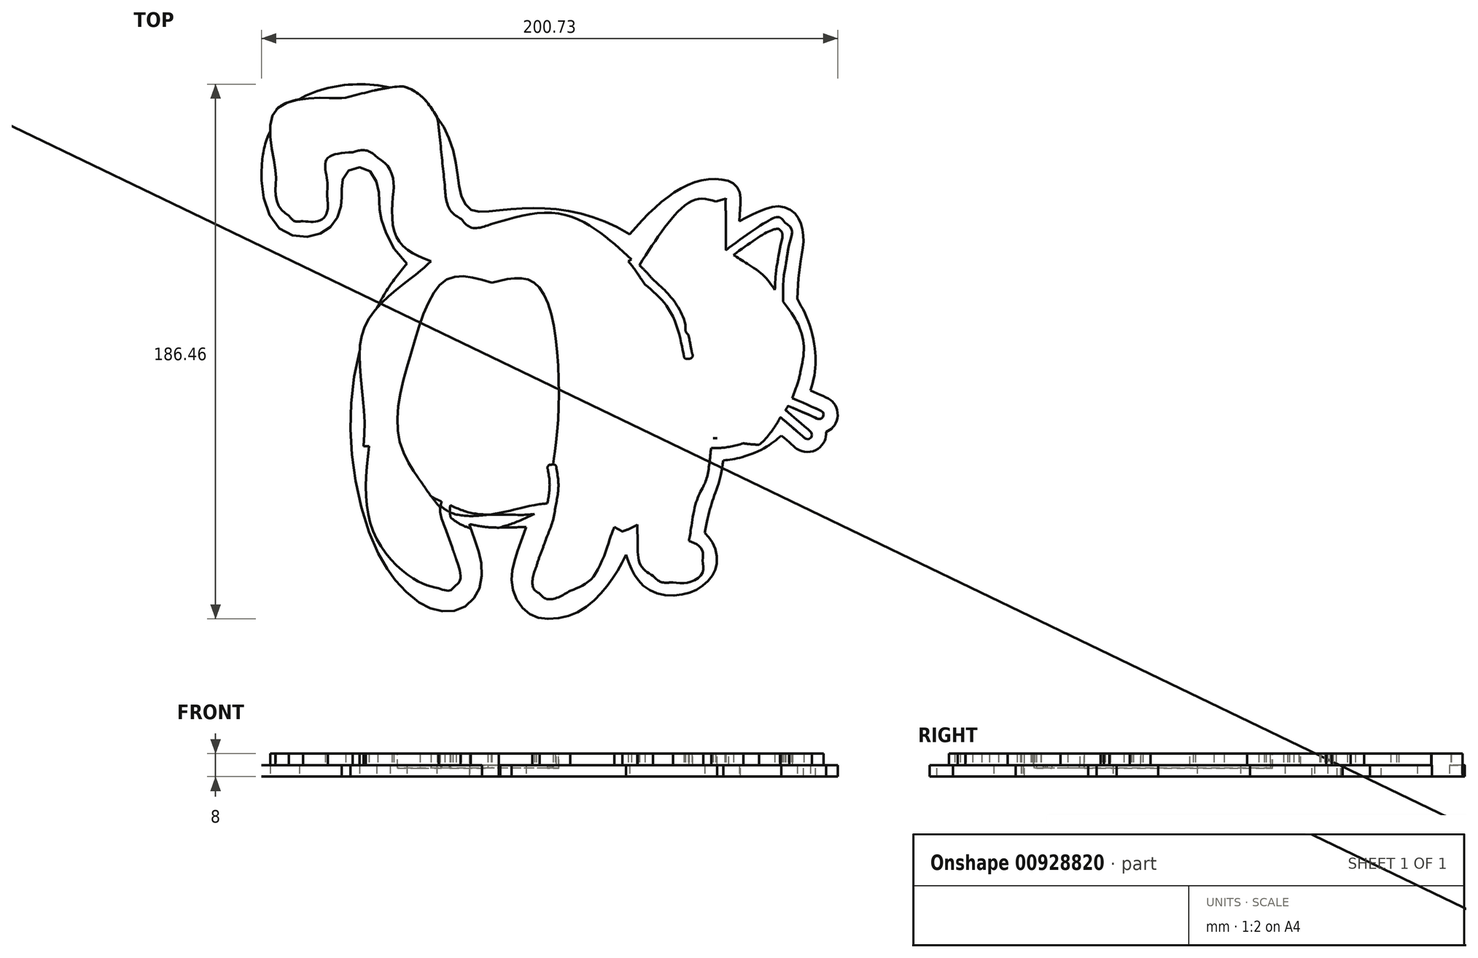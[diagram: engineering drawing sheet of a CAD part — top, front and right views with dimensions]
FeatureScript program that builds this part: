
annotation { "Feature Type Name" : "Feature", "Feature Type Description" : "" }
export const myFeature = defineFeature(function(context is Context, id is Id, definition is map)
    precondition{}
    {
        {
            var Q0;
            Q0=qCreatedBy(makeId("Top.planeOp"),FACE);
            var sketch = newSketch(context, id + "F0", { "sketchPlane" : qUnion([Q0])});
            skFitSpline(sketch, "E0", {"points": [v(100.05, -19.55) * mm, v(99.42, -17.93) * mm, v(98.2, -16.66) * mm, v(96.61, -15.96) * mm, v(96.6, -15.96) * mm, v(96.6, -15.96) * mm, v(90.96, -13.49) * mm, v(90.96, -13.48) * mm, v(90.96, -13.48) * mm, v(91.5, -11.8) * mm, v(91.97, -10.07) * mm, v(92.36, -8.28) * mm]});
            skFitSpline(sketch, "E1", {"points": [v(92.36, -8.28) * mm, v(93.69, 1.04) * mm, v(91.75, 9.81) * mm, v(86.45, 18.47) * mm]});
            skFitSpline(sketch, "E2", {"points": [v(86.45, 18.47) * mm, v(86.5, 20.98) * mm, v(86.7, 25.82) * mm, v(87.33, 29.56) * mm, v(87.33, 29.56) * mm, v(87.33, 29.56) * mm, v(87.49, 30.5) * mm, v(87.49, 30.5) * mm, v(87.49, 30.5) * mm, v(88.6, 37.13) * mm, v(89.76, 43.98) * mm, v(85.52, 48.23) * mm]});
            skFitSpline(sketch, "E3", {"points": [v(85.55, 48.2) * mm, v(84.21, 49.71) * mm, v(82.4, 50.6) * mm, v(80.32, 50.72) * mm, v(77.64, 50.9) * mm, v(74.32, 50.04) * mm, v(66.25, 45.62) * mm, v(66.25, 45.62) * mm, v(66.25, 45.62) * mm, v(66.52, 49.81) * mm, v(66.52, 49.81) * mm, v(66.52, 49.82) * mm, v(66.67, 52.13) * mm, v(66.8, 54.32) * mm, v(66.16, 56.37) * mm]});
            skFitSpline(sketch, "E4", {"points": [v(66.24, 56.23) * mm, v(64.62, 59.16) * mm, v(61.64, 60.58) * mm, v(58.04, 60.13) * mm, v(58.04, 60.13) * mm, v(58.04, 60.13) * mm, v(58.03, 60.13) * mm, v(58.02, 60.13) * mm, v(58.02, 60.13) * mm, v(58.02, 60.13) * mm]});
            skFitSpline(sketch, "E5", {"points": [v(58.04, 60.13) * mm, v(49.37, 60.78) * mm, v(39.5, 54.54) * mm, v(27.98, 41.07) * mm]});
            skFitSpline(sketch, "E6", {"points": [v(27.98, 41.07) * mm, v(17.24, 47.84) * mm, v(5.03, 50.86) * mm, v(-8.4, 50.04) * mm]});
            skFitSpline(sketch, "E7", {"points": [v(-8.4, 50.04) * mm, v(-12.56, 50.04) * mm, v(-16.9, 49.67) * mm, v(-21.3, 48.93) * mm]});
            skFitSpline(sketch, "E8", {"points": [v(-21.3, 48.93) * mm, v(-21.45, 48.9) * mm, v(-22.21, 48.75) * mm, v(-23.26, 48.75) * mm, v(-24.5, 48.75) * mm, v(-26.27, 48.97) * mm, v(-27.72, 49.98) * mm]});
            skFitSpline(sketch, "E9", {"points": [v(-27.72, 49.98) * mm, v(-29.7, 51.36) * mm, v(-30.92, 54.16) * mm, v(-31.35, 58.29) * mm]});
            skFitSpline(sketch, "E10", {"points": [v(-31.35, 58.29) * mm, v(-32.1, 65.45) * mm, v(-33.66, 74.59) * mm, v(-39.08, 81.77) * mm]});
            skFitSpline(sketch, "E11", {"points": [v(-39.08, 81.77) * mm, v(-44.85, 89.43) * mm, v(-53.9, 93.32) * mm, v(-65.99, 93.32) * mm]});
            skFitSpline(sketch, "E12", {"points": [v(-65.99, 93.32) * mm, v(-67.63, 93.32) * mm, v(-69.35, 93.25) * mm, v(-71.11, 93.1) * mm]});
            skFitSpline(sketch, "E13", {"points": [v(-71.11, 93.1) * mm, v(-80.78, 92.94) * mm, v(-100.32, 85.34) * mm, v(-100.32, 62.6) * mm, v(-100.32, 53.34) * mm, v(-98.24, 47) * mm, v(-93.96, 43.22) * mm]});
            skFitSpline(sketch, "E14", {"points": [v(-93.96, 43.22) * mm, v(-90.88, 40.5) * mm, v(-87.7, 40.1) * mm, v(-86.07, 40.1) * mm, v(-85.87, 40.1) * mm, v(-85.7, 40.1) * mm, v(-85.57, 40.1) * mm]});
            skFitSpline(sketch, "E15", {"points": [v(-85.57, 40.1) * mm, v(-77.63, 40.22) * mm, v(-72.32, 45.63) * mm, v(-72.32, 53.6) * mm, v(-72.32, 54) * mm, v(-72.32, 54.42) * mm, v(-72.33, 54.86) * mm]});
            skFitSpline(sketch, "E16", {"points": [v(-72.33, 54.86) * mm, v(-72.4, 60.63) * mm, v(-72, 62.97) * mm, v(-67.3, 64.29) * mm]});
            skFitSpline(sketch, "E17", {"points": [v(-67.3, 64.29) * mm, v(-66.87, 64.37) * mm, v(-66.46, 64.42) * mm, v(-66.06, 64.42) * mm]});
            skFitSpline(sketch, "E18", {"points": [v(-66.06, 64.42) * mm, v(-64.87, 64.42) * mm, v(-63.8, 64.03) * mm, v(-62.8, 63.22) * mm]});
            skFitSpline(sketch, "E19", {"points": [v(-62.8, 63.22) * mm, v(-60.65, 61.5) * mm, v(-59.32, 58.2) * mm, v(-59.32, 54.6) * mm, v(-59.32, 43.94) * mm, v(-55.96, 35.93) * mm, v(-49.09, 30.32) * mm]});
            skFitSpline(sketch, "E20", {"points": [v(-49.06, 31.26) * mm, v(-56.9, 22.68) * mm, v(-69.3, 4.66) * mm, v(-69.3, -23.45) * mm, v(-69.3, -65.04) * mm, v(-52.28, -85.8) * mm, v(-40.85, -89.61) * mm]});
            skFitSpline(sketch, "E21", {"points": [v(-40.85, -89.61) * mm, v(-39, -90.23) * mm, v(-37.21, -90.54) * mm, v(-35.54, -90.54) * mm]});
            skFitSpline(sketch, "E22", {"points": [v(-35.54, -90.54) * mm, v(-31.43, -90.54) * mm, v(-28.77, -88.74) * mm, v(-27.26, -87.23) * mm, v(-22.51, -82.48) * mm, v(-22.87, -74.65) * mm, v(-24.62, -69.4) * mm]});
            skFitSpline(sketch, "E23", {"points": [v(-24.62, -69.4) * mm, v(-24.96, -68.4) * mm, v(-25.35, -67.28) * mm, v(-25.77, -66.08) * mm]});
            skFitSpline(sketch, "E24", {"points": [v(-25.77, -66.08) * mm, v(-26.27, -64.66) * mm, v(-27.07, -62.37) * mm, v(-27.8, -60.06) * mm]});
            skFitSpline(sketch, "E25", {"points": [v(-27.81, -60.06) * mm, v(-23.36, -60.89) * mm, v(-18.46, -61.28) * mm, v(-13.17, -61.24) * mm, v(-11.35, -61.22) * mm, v(-9.62, -61.15) * mm, v(-8.01, -61.05) * mm]});
            skFitSpline(sketch, "E26", {"points": [v(-8.01, -61.05) * mm, v(-8.45, -62.3) * mm, v(-8.91, -63.53) * mm, v(-9.36, -64.74) * mm]});
            skFitSpline(sketch, "E27", {"points": [v(-9.36, -64.74) * mm, v(-10.33, -67.35) * mm, v(-11.25, -69.8) * mm, v(-12.03, -72.4) * mm]});
            skFitSpline(sketch, "E28", {"points": [v(-12.03, -72.4) * mm, v(-14.3, -79.95) * mm, v(-12.89, -86.47) * mm, v(-8.18, -90.3) * mm]});
            skFitSpline(sketch, "E29", {"points": [v(-8.18, -90.3) * mm, v(-6.56, -91.6) * mm, v(-3.77, -93.17) * mm, v(0.34, -93.17) * mm, v(3.74, -93.17) * mm, v(7.45, -92.08) * mm, v(11.4, -89.93) * mm]});
            skFitSpline(sketch, "E30", {"points": [v(11.4, -89.93) * mm, v(18.3, -85.62) * mm, v(23.55, -77.3) * mm, v(26.85, -70.76) * mm]});
            skFitSpline(sketch, "E31", {"points": [v(26.85, -70.76) * mm, v(27.9, -74.84) * mm, v(29.69, -78.7) * mm, v(32.65, -81.38) * mm]});
            skFitSpline(sketch, "E32", {"points": [v(32.65, -81.38) * mm, v(35.24, -83.73) * mm, v(38.48, -84.97) * mm, v(42, -84.97) * mm, v(42.42, -84.97) * mm, v(42.84, -84.95) * mm, v(43.26, -84.92) * mm]});
            skFitSpline(sketch, "E33", {"points": [v(43.26, -84.92) * mm, v(51.65, -84.78) * mm, v(58.45, -79.2) * mm, v(58.45, -72.42) * mm, v(58.45, -68.76) * mm, v(56.88, -65.47) * mm, v(54.13, -63.1) * mm]});
            skFitSpline(sketch, "E34", {"points": [v(54.13, -63.1) * mm, v(54.92, -59.03) * mm, v(56.29, -52.8) * mm, v(57.92, -48.98) * mm]});
            skFitSpline(sketch, "E35", {"points": [v(57.92, -48.98) * mm, v(59.23, -45.93) * mm, v(60.1, -41.73) * mm, v(60.66, -37.87) * mm]});
            skFitSpline(sketch, "E36", {"points": [v(60.66, -37.87) * mm, v(65.8, -37.43) * mm, v(73.93, -35.63) * mm, v(80.9, -29.2) * mm, v(80.9, -29.2) * mm, v(80.9, -29.2) * mm, v(85.7, -33.34) * mm, v(85.7, -33.34) * mm, v(85.7, -33.34) * mm, v(86.88, -34.36) * mm, v(88.39, -34.92) * mm, v(89.94, -34.92) * mm, v(91.84, -34.92) * mm, v(93.63, -34.1) * mm, v(94.87, -32.66) * mm]});
            skFitSpline(sketch, "E37", {"points": [v(94.87, -32.66) * mm, v(96, -31.35) * mm, v(96.56, -29.68) * mm, v(96.43, -27.94) * mm]});
            skFitSpline(sketch, "E38", {"points": [v(96.43, -27.94) * mm, v(97.98, -27.32) * mm, v(99.26, -26.1) * mm, v(99.95, -24.52) * mm]});
            skFitSpline(sketch, "E39", {"points": [v(99.95, -24.52) * mm, v(100.65, -22.93) * mm, v(100.69, -21.17) * mm, v(100.05, -19.55) * mm]});
            skFitSpline(sketch, "E40", {"points": [v(-20, 24.09) * mm, v(-36, 25.09) * mm, v(-48, 0.09) * mm, v(-51.98, -31.79) * mm, v(-45.1, -44.74) * mm, v(-45, -44.91) * mm, v(-45, -44.91) * mm, v(-45, -44.91) * mm]});
            skFitSpline(sketch, "E41", {"points": [v(-45, -44.91) * mm, v(-45, -44.91) * mm, v(-45, -44.91) * mm, v(-44.81, -45.11) * mm, v(-30.47, -60.36) * mm, v(0.64, -53.66) * mm]});
            skFitSpline(sketch, "E42", {"points": [v(0.64, -53.66) * mm, v(2, -48.91) * mm, v(1, -40.92) * mm, v(1, -40.91) * mm, v(1, -40.91) * mm, v(3, -24.9) * mm, v(-4, 23.09) * mm, v(-20, 24.09) * mm]});
            skFitSpline(sketch, "E43", {"points": [v(94.6, -20.54) * mm, v(94.6, -20.54) * mm, v(94.6, -20.54) * mm, v(94.34, -20.43) * mm, v(84.57, -16.14) * mm, v(84.57, -16.14) * mm, v(84.57, -16.14) * mm, v(85.75, -13.56) * mm, v(86.74, -10.62) * mm, v(87.47, -7.23) * mm, v(87.47, -7.2) * mm, v(87.48, -7.16) * mm, v(87.49, -7.13) * mm]});
            skFitSpline(sketch, "E44", {"points": [v(87.49, -7.13) * mm, v(88.7, 1.43) * mm, v(86.75, 9.5) * mm, v(81.5, 17.52) * mm]});
            skFitSpline(sketch, "E45", {"points": [v(81.5, 17.52) * mm, v(81.52, 19.24) * mm, v(81.64, 25.8) * mm, v(82.48, 30.84) * mm, v(82.48, 30.84) * mm, v(82.48, 30.84) * mm, v(82.64, 31.78) * mm, v(82.64, 31.78) * mm, v(82.64, 31.78) * mm, v(83.55, 37.16) * mm, v(84.48, 42.72) * mm, v(82.06, 45.15) * mm]});
            skFitSpline(sketch, "E46", {"points": [v(82.06, 45.15) * mm, v(80.3, 46.9) * mm, v(76.8, 46.02) * mm, v(62.53, 36.26) * mm]});
            skFitSpline(sketch, "E47", {"points": [v(62.54, 36.27) * mm, v(62.14, 36) * mm, v(61.8, 35.76) * mm, v(61.52, 35.57) * mm, v(61.51, 35.57) * mm, v(61.51, 35.62) * mm, v(61.5, 49.1) * mm, v(61.5, 49.1) * mm, v(61.5, 49.1) * mm, v(61.49, 53.01) * mm, v(61.48, 55.6) * mm, v(57.98, 55.59) * mm, v(57.87, 55.59) * mm, v(57.74, 55.6) * mm, v(57.57, 55.62) * mm]});
            skFitSpline(sketch, "E48", {"points": [v(57.59, 55.61) * mm, v(54.51, 55.88) * mm, v(45.27, 56.66) * mm, v(28.65, 32.24) * mm]});
            skFitSpline(sketch, "E49", {"points": [v(28.65, 32.24) * mm, v(18.35, 41.12) * mm, v(2.62, 48.38) * mm, v(-20.25, 44.57) * mm]});
            skFitSpline(sketch, "E50", {"points": [v(-20.25, 44.57) * mm, v(-20.3, 44.55) * mm, v(-26.05, 43.17) * mm, v(-30.65, 46.38) * mm]});
            skFitSpline(sketch, "E51", {"points": [v(-30.65, 46.38) * mm, v(-33.87, 48.63) * mm, v(-35.8, 52.63) * mm, v(-36.4, 58.27) * mm]});
            skFitSpline(sketch, "E52", {"points": [v(-36.4, 58.27) * mm, v(-38.1, 74.54) * mm, v(-43.55, 90.86) * mm, v(-70.95, 88.61) * mm]});
            skFitSpline(sketch, "E53", {"points": [v(-70.95, 88.61) * mm, v(-76.22, 88.57) * mm, v(-95.38, 84.2) * mm, v(-95.38, 63.11) * mm, v(-95.38, 55.46) * mm, v(-93.81, 50.2) * mm, v(-90.72, 47.47) * mm]});
            skFitSpline(sketch, "E54", {"points": [v(-90.72, 47.47) * mm, v(-88.54, 45.55) * mm, v(-86.37, 45.57) * mm, v(-85.81, 45.61) * mm]});
            skFitSpline(sketch, "E55", {"points": [v(-85.81, 45.61) * mm, v(-80.53, 45.64) * mm, v(-77.38, 48.81) * mm, v(-77.38, 54.11) * mm, v(-77.38, 54.48) * mm, v(-77.39, 54.88) * mm, v(-77.4, 55.3) * mm]});
            skFitSpline(sketch, "E56", {"points": [v(-77.4, 55.3) * mm, v(-77.46, 60.31) * mm, v(-77.56, 67.19) * mm, v(-68.56, 69.65) * mm]});
            skFitSpline(sketch, "E57", {"points": [v(-68.56, 69.65) * mm, v(-65.33, 70.36) * mm, v(-62.28, 69.66) * mm, v(-59.74, 67.63) * mm]});
            skFitSpline(sketch, "E58", {"points": [v(-59.74, 67.63) * mm, v(-56.39, 64.94) * mm, v(-54.38, 60.26) * mm, v(-54.38, 55.11) * mm, v(-54.38, 43.67) * mm, v(-50.32, 36.34) * mm, v(-41.25, 31.6) * mm]});
            skFitSpline(sketch, "E59", {"points": [v(-41.25, 31.6) * mm, v(-47.13, 26.46) * mm, v(-64.38, 8.6) * mm, v(-64.38, -23.89) * mm, v(-64.38, -62.56) * mm, v(-49.03, -82.09) * mm, v(-39.36, -85.31) * mm]});
            skFitSpline(sketch, "E60", {"points": [v(-39.36, -85.31) * mm, v(-37.93, -85.79) * mm, v(-36.7, -85.98) * mm, v(-35.63, -85.98) * mm]});
            skFitSpline(sketch, "E61", {"points": [v(-35.63, -85.98) * mm, v(-33.33, -85.98) * mm, v(-31.83, -85.07) * mm, v(-30.9, -84.14) * mm]});
            skFitSpline(sketch, "E62", {"points": [v(-30.9, -84.14) * mm, v(-27.95, -81.2) * mm, v(-28.05, -75.63) * mm, v(-29.46, -71.42) * mm]});
            skFitSpline(sketch, "E63", {"points": [v(-29.46, -71.42) * mm, v(-29.78, -70.45) * mm, v(-30.17, -69.35) * mm, v(-30.58, -68.18) * mm]});
            skFitSpline(sketch, "E64", {"points": [v(-30.58, -68.18) * mm, v(-32.12, -63.8) * mm, v(-34.53, -56.92) * mm, v(-34.48, -53.5) * mm]});
            skFitSpline(sketch, "E65", {"points": [v(-34.48, -53.5) * mm, v(-27.6, -56.08) * mm, v(-19.8, -56.8) * mm, v(-13.26, -56.8) * mm, v(-8.06, -56.8) * mm, v(-3.66, -56.36) * mm, v(-1.16, -56.03) * mm]});
            skFitSpline(sketch, "E66", {"points": [v(-1.16, -56.03) * mm, v(-2.09, -59.9) * mm, v(-3.43, -63.54) * mm, v(-4.76, -67.1) * mm]});
            skFitSpline(sketch, "E67", {"points": [v(-4.76, -67.1) * mm, v(-5.7, -69.63) * mm, v(-6.58, -72) * mm, v(-7.32, -74.46) * mm]});
            skFitSpline(sketch, "E68", {"points": [v(-7.32, -74.46) * mm, v(-8.97, -79.97) * mm, v(-8.17, -84.55) * mm, v(-5.1, -87.03) * mm]});
            skFitSpline(sketch, "E69", {"points": [v(-5.1, -87.03) * mm, v(-4.1, -87.85) * mm, v(-2.37, -88.79) * mm, v(0.26, -88.79) * mm, v(2.47, -88.79) * mm, v(5.32, -88.12) * mm, v(8.91, -86.16) * mm]});
            skFitSpline(sketch, "E70", {"points": [v(8.91, -86.16) * mm, v(17.59, -80.74) * mm, v(23.66, -67.02) * mm, v(25.43, -62.65) * mm]});
            skFitSpline(sketch, "E71", {"points": [v(25.43, -62.65) * mm, v(26.4, -62.3) * mm, v(28.3, -61.54) * mm, v(30.64, -60.24) * mm]});
            skFitSpline(sketch, "E72", {"points": [v(30.64, -60.24) * mm, v(30.76, -65.7) * mm, v(31.73, -74.12) * mm, v(36.18, -78.15) * mm]});
            skFitSpline(sketch, "E73", {"points": [v(36.18, -78.15) * mm, v(37.86, -79.67) * mm, v(39.87, -80.44) * mm, v(42.17, -80.44) * mm, v(42.5, -80.44) * mm, v(42.85, -80.42) * mm, v(43.2, -80.39) * mm]});
            skFitSpline(sketch, "E74", {"points": [v(43.05, -80.4) * mm, v(48.7, -80.36) * mm, v(53.47, -76.94) * mm, v(53.47, -72.9) * mm, v(53.47, -69.83) * mm, v(51.73, -67.35) * mm, v(48.65, -65.94) * mm]});
            skFitSpline(sketch, "E75", {"points": [v(48.68, -65.95) * mm, v(49.24, -62.62) * mm, v(51, -53.03) * mm, v(53.38, -47.5) * mm]});
            skFitSpline(sketch, "E76", {"points": [v(53.38, -47.5) * mm, v(54.77, -44.33) * mm, v(55.79, -39) * mm, v(56.4, -33.46) * mm]});
            skFitSpline(sketch, "E77", {"points": [v(56.3, -33.48) * mm, v(56.63, -33.5) * mm, v(57.14, -33.53) * mm, v(57.8, -33.53) * mm, v(62.2, -33.52) * mm, v(72.96, -32.44) * mm, v(80.57, -22.78) * mm, v(80.57, -22.78) * mm, v(80.57, -22.78) * mm, v(89.02, -30.05) * mm, v(89.02, -30.05) * mm, v(89.02, -30.05) * mm, v(89.3, -30.3) * mm, v(89.66, -30.42) * mm, v(90, -30.42) * mm, v(90.42, -30.41) * mm, v(90.84, -30.24) * mm, v(91.14, -29.9) * mm]});
            skFitSpline(sketch, "E78", {"points": [v(91.14, -29.9) * mm, v(91.68, -29.27) * mm, v(91.6, -28.33) * mm, v(90.98, -27.78) * mm, v(90.98, -27.78) * mm, v(90.96, -27.76) * mm, v(82.35, -20.33) * mm, v(82.33, -20.3) * mm, v(82.33, -20.3) * mm, v(82.63, -19.83) * mm, v(82.93, -19.34) * mm, v(83.21, -18.83) * mm, v(83.21, -18.83) * mm, v(83.24, -18.84) * mm, v(93.38, -23.28) * mm, v(93.4, -23.29) * mm, v(93.4, -23.3) * mm, v(93.6, -23.37) * mm, v(93.8, -23.41) * mm, v(94, -23.41) * mm, v(94.58, -23.41) * mm, v(95.13, -23.08) * mm, v(95.37, -22.52) * mm]});
            skFitSpline(sketch, "E79", {"points": [v(95.37, -22.52) * mm, v(95.7, -21.76) * mm, v(95.36, -20.87) * mm, v(94.6, -20.54) * mm]});
            skFitSpline(sketch, "E80", {"points": [v(80.08, 42.86) * mm, v(81.2, 41.27) * mm, v(80.3, 35.9) * mm, v(79.68, 32.29) * mm, v(79.68, 32.28) * mm, v(79.68, 32.28) * mm, v(79.52, 31.33) * mm, v(79.52, 31.33) * mm, v(79.52, 31.33) * mm, v(78.99, 28.14) * mm, v(78.74, 24.46) * mm, v(78.61, 21.63) * mm]});
            skFitSpline(sketch, "E81", {"points": [v(78.66, 21.58) * mm, v(74.42, 26.84) * mm, v(68.01, 31.38) * mm, v(64.2, 33.82) * mm]});
            skFitSpline(sketch, "E82", {"points": [v(64.2, 33.82) * mm, v(75.54, 41.54) * mm, v(79.02, 42.85) * mm, v(80.08, 42.86) * mm]});
            skFitSpline(sketch, "E83", {"points": [v(56.8, -30.09) * mm, v(57.45, -24.16) * mm, v(57.63, -18.41) * mm, v(57.21, -15.3) * mm]});
            skFitSpline(sketch, "E84", {"points": [v(57.21, -15.3) * mm, v(57.08, -14.48) * mm, v(56.3, -13.92) * mm, v(55.49, -14.06) * mm]});
            skFitSpline(sketch, "E85", {"points": [v(55.49, -14.06) * mm, v(54.67, -14.2) * mm, v(54.12, -14.98) * mm, v(54.26, -15.8) * mm]});
            skFitSpline(sketch, "E86", {"points": [v(54.26, -15.8) * mm, v(55.17, -21.85) * mm, v(53.8, -39.35) * mm, v(50.85, -45.9) * mm]});
            skFitSpline(sketch, "E87", {"points": [v(50.85, -45.9) * mm, v(47.84, -53) * mm, v(45.9, -65.75) * mm, v(45.82, -66.29) * mm]});
            skFitSpline(sketch, "E88", {"points": [v(45.82, -66.29) * mm, v(45.7, -67) * mm, v(46.13, -67.7) * mm, v(46.82, -67.94) * mm]});
            skFitSpline(sketch, "E89", {"points": [v(46.56, -67.86) * mm, v(48.39, -68.4) * mm, v(50.59, -69.63) * mm, v(50.67, -72.31) * mm, v(50.73, -74.4) * mm, v(47.53, -76.91) * mm, v(43.31, -77.04) * mm, v(43.26, -77.04) * mm, v(43.21, -77.04) * mm, v(43.16, -77.05) * mm]});
            skFitSpline(sketch, "E90", {"points": [v(43.16, -77.05) * mm, v(41.26, -77.26) * mm, v(39.69, -76.8) * mm, v(38.37, -75.63) * mm]});
            skFitSpline(sketch, "E91", {"points": [v(38.37, -75.63) * mm, v(34.21, -71.92) * mm, v(33.7, -62.5) * mm, v(33.67, -58.63) * mm, v(33.67, -58.48) * mm, v(33.64, -58.34) * mm, v(33.6, -58.21) * mm]});
            skFitSpline(sketch, "E92", {"points": [v(33.6, -58.21) * mm, v(39.18, -54.54) * mm, v(45.84, -48.25) * mm, v(48.71, -38.1) * mm]});
            skFitSpline(sketch, "E93", {"points": [v(48.71, -38.1) * mm, v(48.93, -37.3) * mm, v(48.46, -36.48) * mm, v(47.67, -36.26) * mm]});
            skFitSpline(sketch, "E94", {"points": [v(47.67, -36.26) * mm, v(46.87, -36.04) * mm, v(46.04, -36.5) * mm, v(45.82, -37.3) * mm]});
            skFitSpline(sketch, "E95", {"points": [v(45.82, -37.3) * mm, v(42.3, -49.82) * mm, v(32.13, -56.07) * mm, v(26.98, -58.5) * mm]});
            skFitSpline(sketch, "E96", {"points": [v(26.98, -58.5) * mm, v(29.59, -51.06) * mm, v(34.55, -34.09) * mm, v(30.56, -22.16) * mm]});
            skFitSpline(sketch, "E97", {"points": [v(30.56, -22.16) * mm, v(30.3, -21.38) * mm, v(29.45, -20.95) * mm, v(28.66, -21.2) * mm]});
            skFitSpline(sketch, "E98", {"points": [v(28.66, -21.2) * mm, v(27.88, -21.47) * mm, v(27.45, -22.32) * mm, v(27.71, -23.1) * mm]});
            skFitSpline(sketch, "E99", {"points": [v(27.71, -23.1) * mm, v(32.46, -37.4) * mm, v(22.82, -60.81) * mm, v(22.72, -61.07) * mm]});
            skFitSpline(sketch, "E100", {"points": [v(22.72, -61.07) * mm, v(21.58, -63.88) * mm, v(15.49, -78.18) * mm, v(7.31, -83.25) * mm]});
            skFitSpline(sketch, "E101", {"points": [v(7.31, -83.25) * mm, v(2.74, -85.73) * mm, v(-1.13, -86.12) * mm, v(-3.3, -84.34) * mm]});
            skFitSpline(sketch, "E102", {"points": [v(-3.3, -84.34) * mm, v(-5.34, -82.68) * mm, v(-5.8, -79.18) * mm, v(-4.52, -74.96) * mm]});
            skFitSpline(sketch, "E103", {"points": [v(-4.52, -74.96) * mm, v(-3.81, -72.6) * mm, v(-2.94, -70.26) * mm, v(-2.02, -67.79) * mm]});
            skFitSpline(sketch, "E104", {"points": [v(-2.02, -67.79) * mm, v(-0.49, -63.65) * mm, v(1.16, -59.22) * mm, v(2.11, -54.3) * mm]});
            skFitSpline(sketch, "E105", {"points": [v(2.11, -54.3) * mm, v(2.9, -50.13) * mm, v(3.19, -45.6) * mm, v(2.47, -40.61) * mm]});
            skFitSpline(sketch, "E106", {"points": [v(2.47, -40.61) * mm, v(2.36, -39.8) * mm, v(1.6, -39.22) * mm, v(0.78, -39.34) * mm]});
            skFitSpline(sketch, "E107", {"points": [v(0.78, -39.34) * mm, v(-0.04, -39.46) * mm, v(-0.61, -40.22) * mm, v(-0.5, -41.04) * mm]});
            skFitSpline(sketch, "E108", {"points": [v(-0.5, -41.04) * mm, v(0.12, -45.32) * mm, v(-0.05, -49.2) * mm, v(-0.66, -52.85) * mm]});
            skFitSpline(sketch, "E109", {"points": [v(-0.66, -52.85) * mm, v(-6.2, -53.62) * mm, v(-32.84, -56.57) * mm, v(-43.87, -43.83) * mm]});
            skFitSpline(sketch, "E110", {"points": [v(-43.87, -43.83) * mm, v(-44.4, -43.2) * mm, v(-45.36, -43.14) * mm, v(-45.98, -43.68) * mm]});
            skFitSpline(sketch, "E111", {"points": [v(-45.98, -43.68) * mm, v(-46.6, -44.22) * mm, v(-46.68, -45.17) * mm, v(-46.13, -45.8) * mm]});
            skFitSpline(sketch, "E112", {"points": [v(-46.13, -45.8) * mm, v(-43.75, -48.54) * mm, v(-40.77, -50.63) * mm, v(-37.48, -52.2) * mm]});
            skFitSpline(sketch, "E113", {"points": [v(-37.48, -52.2) * mm, v(-38.03, -55.8) * mm, v(-36.09, -61.8) * mm, v(-33.53, -69.1) * mm]});
            skFitSpline(sketch, "E114", {"points": [v(-33.53, -69.1) * mm, v(-33.12, -70.25) * mm, v(-32.74, -71.33) * mm, v(-32.42, -72.29) * mm]});
            skFitSpline(sketch, "E115", {"points": [v(-32.42, -72.29) * mm, v(-31.34, -75.54) * mm, v(-31.22, -80.03) * mm, v(-33.14, -81.94) * mm, v(-34.25, -83.06) * mm, v(-36.07, -83.2) * mm, v(-38.53, -82.39) * mm]});
            skFitSpline(sketch, "E116", {"points": [v(-38.5, -82.4) * mm, v(-46, -79.9) * mm, v(-61.48, -62.3) * mm, v(-61.48, -23.82) * mm]});
            skFitSpline(sketch, "E117", {"points": [v(-61.48, -23.82) * mm, v(-61.48, 9.58) * mm, v(-42, 27.26) * mm, v(-38.28, 30.32) * mm]});
            skFitSpline(sketch, "E118", {"points": [v(-38.28, 30.32) * mm, v(-34.83, 29.12) * mm, v(-25.05, 26.34) * mm, v(-16.42, 29.79) * mm]});
            skFitSpline(sketch, "E119", {"points": [v(-16.42, 29.79) * mm, v(-15.65, 30.1) * mm, v(-15.28, 30.97) * mm, v(-15.59, 31.74) * mm]});
            skFitSpline(sketch, "E120", {"points": [v(-15.59, 31.74) * mm, v(-15.9, 32.5) * mm, v(-16.77, 32.88) * mm, v(-17.54, 32.57) * mm]});
            skFitSpline(sketch, "E121", {"points": [v(-17.54, 32.57) * mm, v(-25.95, 29.2) * mm, v(-36.14, 32.71) * mm, v(-38.05, 33.42) * mm]});
            skFitSpline(sketch, "E122", {"points": [v(-38.05, 33.42) * mm, v(-38.05, 33.43) * mm, v(-38.05, 33.43) * mm, v(-38.06, 33.43) * mm]});
            skFitSpline(sketch, "E123", {"points": [v(-38.05, 33.42) * mm, v(-47.24, 37.6) * mm, v(-51.17, 44.08) * mm, v(-51.17, 55.06) * mm, v(-51.17, 61.1) * mm, v(-53.59, 66.66) * mm, v(-57.65, 69.92) * mm]});
            skFitSpline(sketch, "E124", {"points": [v(-57.65, 69.92) * mm, v(-60.88, 72.5) * mm, v(-64.9, 73.43) * mm, v(-69.06, 72.5) * mm]});
            skFitSpline(sketch, "E125", {"points": [v(-69.06, 72.5) * mm, v(-80.37, 69.42) * mm, v(-80.25, 60.17) * mm, v(-80.18, 55.2) * mm]});
            skFitSpline(sketch, "E126", {"points": [v(-80.18, 55.2) * mm, v(-80.17, 54.8) * mm, v(-80.17, 54.42) * mm, v(-80.17, 54.06) * mm, v(-80.17, 50.36) * mm, v(-81.97, 48.56) * mm, v(-85.67, 48.56) * mm, v(-85.7, 48.56) * mm, v(-85.78, 48.55) * mm, v(-85.82, 48.55) * mm]});
            skFitSpline(sketch, "E127", {"points": [v(-85.82, 48.55) * mm, v(-85.88, 48.54) * mm, v(-87.2, 48.45) * mm, v(-88.6, 49.74) * mm]});
            skFitSpline(sketch, "E128", {"points": [v(-88.6, 49.74) * mm, v(-90.22, 51.23) * mm, v(-92.16, 54.75) * mm, v(-92.17, 63.05) * mm, v(-92.18, 84.23) * mm, v(-70.9, 85.56) * mm, v(-70.68, 85.56) * mm, v(-70.63, 85.56) * mm, v(-70.6, 85.56) * mm, v(-70.55, 85.57) * mm]});
            skFitSpline(sketch, "E129", {"points": [v(-70.55, 85.57) * mm, v(-47.13, 87.51) * mm, v(-41.06, 75.92) * mm, v(-39.17, 57.9) * mm]});
            skFitSpline(sketch, "E130", {"points": [v(-39.17, 57.9) * mm, v(-38.48, 51.36) * mm, v(-36.13, 46.64) * mm, v(-32.17, 43.87) * mm]});
            skFitSpline(sketch, "E131", {"points": [v(-32.17, 43.87) * mm, v(-26.69, 40.04) * mm, v(-20.15, 41.4) * mm, v(-19.38, 41.59) * mm]});
            skFitSpline(sketch, "E132", {"points": [v(-19.38, 41.59) * mm, v(2.4, 45.2) * mm, v(20.14, 39.14) * mm, v(33.36, 23.55) * mm]});
            skFitSpline(sketch, "E133", {"points": [v(33.36, 23.55) * mm, v(43.3, 11.83) * mm, v(46.85, -1.19) * mm, v(46.88, -1.32) * mm]});
            skFitSpline(sketch, "E134", {"points": [v(46.88, -1.32) * mm, v(47.06, -1.99) * mm, v(47.67, -2.43) * mm, v(48.33, -2.43) * mm, v(48.46, -2.43) * mm, v(48.59, -2.42) * mm, v(48.71, -2.38) * mm]});
            skFitSpline(sketch, "E135", {"points": [v(48.71, -2.38) * mm, v(49.52, -2.17) * mm, v(50, -1.35) * mm, v(49.78, -0.55) * mm]});
            skFitSpline(sketch, "E136", {"points": [v(49.78, -0.55) * mm, v(49.64, 0) * mm, v(46.15, 13.19) * mm, v(35.86, 25.48) * mm]});
            skFitSpline(sketch, "E137", {"points": [v(35.86, 25.48) * mm, v(34.52, 27.07) * mm, v(33.03, 28.69) * mm, v(31.38, 30.28) * mm]});
            skFitSpline(sketch, "E138", {"points": [v(31.38, 30.28) * mm, v(41.99, 45.66) * mm, v(50.95, 53.14) * mm, v(58, 52.47) * mm]});
            skFitSpline(sketch, "E139", {"points": [v(58, 52.47) * mm, v(58.17, 51.97) * mm, v(58.18, 50.46) * mm, v(58.2, 49) * mm, v(58.2, 48.99) * mm, v(58.2, 48.98) * mm, v(58.35, 34.02) * mm, v(58.35, 34) * mm, v(58.35, 33.99) * mm, v(58.36, 33.43) * mm, v(58.67, 32.93) * mm, v(59.16, 32.68) * mm]});
            skFitSpline(sketch, "E140", {"points": [v(59.16, 32.68) * mm, v(59.3, 32.6) * mm, v(73.92, 24.94) * mm, v(78.75, 16.5) * mm, v(78.77, 16.46) * mm, v(78.79, 16.43) * mm, v(78.8, 16.4) * mm]});
            skFitSpline(sketch, "E141", {"points": [v(78.8, 16.4) * mm, v(83.91, 8.97) * mm, v(85.9, 1.5) * mm, v(84.9, -6.42) * mm]});
            skFitSpline(sketch, "E142", {"points": [v(84.9, -6.42) * mm, v(79.45, -31.1) * mm, v(59.83, -30.35) * mm, v(56.8, -30.09) * mm]});
            skFitSpline(sketch, "E143", {"points": [v(76.5, 4.59) * mm, v(74.84, 4.59) * mm, v(73.5, 2.8) * mm, v(73.5, 0.59) * mm, v(73.5, -1.62) * mm, v(74.84, -3.41) * mm, v(76.5, -3.41) * mm, v(78.16, -3.41) * mm, v(79.5, -1.62) * mm, v(79.5, 0.59) * mm, v(79.5, 2.8) * mm, v(78.16, 4.59) * mm, v(76.5, 4.59) * mm]});
            skFitSpline(sketch, "E144", {"points": [v(51, 13.59) * mm, v(49.07, 13.59) * mm, v(47.5, 11.8) * mm, v(47.5, 9.59) * mm, v(47.5, 7.38) * mm, v(49.07, 5.59) * mm, v(51, 5.59) * mm, v(52.93, 5.59) * mm, v(54.5, 7.38) * mm, v(54.5, 9.59) * mm, v(54.5, 11.8) * mm, v(52.93, 13.59) * mm, v(51, 13.59) * mm]});
            skFitSpline(sketch, "E145", {"points": [v(71.41, -3.47) * mm, v(70.62, -3.25) * mm, v(69.79, -3.7) * mm, v(69.56, -4.5) * mm]});
            skFitSpline(sketch, "E146", {"points": [v(69.56, -4.49) * mm, v(69.2, -5.75) * mm, v(68.86, -6.15) * mm, v(68.74, -6.26) * mm]});
            skFitSpline(sketch, "E147", {"points": [v(68.74, -6.26) * mm, v(68.2, -6.08) * mm, v(67.05, -4.63) * mm, v(66.34, -3.23) * mm]});
            skFitSpline(sketch, "E148", {"points": [v(66.34, -3.23) * mm, v(66.13, -2.8) * mm, v(65.72, -2.5) * mm, v(65.24, -2.42) * mm]});
            skFitSpline(sketch, "E149", {"points": [v(65.24, -2.42) * mm, v(64.77, -2.34) * mm, v(64.28, -2.5) * mm, v(63.94, -2.84) * mm]});
            skFitSpline(sketch, "E150", {"points": [v(63.94, -2.84) * mm, v(62.31, -4.47) * mm, v(60.88, -5.29) * mm, v(60.1, -5.02) * mm]});
            skFitSpline(sketch, "E151", {"points": [v(60.1, -5.02) * mm, v(59.23, -4.71) * mm, v(58.63, -2.88) * mm, v(58.5, -1.73) * mm]});
            skFitSpline(sketch, "E152", {"points": [v(58.5, -1.73) * mm, v(58.45, -1.32) * mm, v(58.24, -0.97) * mm, v(57.94, -0.73) * mm]});
            skFitSpline(sketch, "E153", {"points": [v(57.94, -0.73) * mm, v(57.64, -0.49) * mm, v(57.25, -0.36) * mm, v(56.84, -0.41) * mm]});
            skFitSpline(sketch, "E154", {"points": [v(56.84, -0.41) * mm, v(56.02, -0.5) * mm, v(55.42, -1.24) * mm, v(55.51, -2.07) * mm]});
            skFitSpline(sketch, "E155", {"points": [v(55.51, -2.07) * mm, v(55.57, -2.55) * mm, v(56.12, -6.8) * mm, v(59.11, -7.85) * mm]});
            skFitSpline(sketch, "E156", {"points": [v(59.11, -7.85) * mm, v(60.74, -8.42) * mm, v(62.6, -7.88) * mm, v(64.64, -6.25) * mm]});
            skFitSpline(sketch, "E157", {"points": [v(64.64, -6.25) * mm, v(65.59, -7.66) * mm, v(67.05, -9.28) * mm, v(68.79, -9.29) * mm, v(68.87, -9.29) * mm, v(68.96, -9.28) * mm, v(69.05, -9.27) * mm]});
            skFitSpline(sketch, "E158", {"points": [v(69.05, -9.27) * mm, v(70.6, -9.13) * mm, v(71.74, -7.8) * mm, v(72.44, -5.33) * mm]});
            skFitSpline(sketch, "E159", {"points": [v(72.44, -5.33) * mm, v(72.67, -4.53) * mm, v(72.2, -3.7) * mm, v(71.41, -3.47) * mm]});
            skFitSpline(sketch, "E160", {"points": [v(-14.88, 11.58) * mm, v(-15.48, 11.63) * mm, v(-18.27, 11.83) * mm, v(-21.45, 11.48) * mm]});
            skFitSpline(sketch, "E161", {"points": [v(-21.45, 11.48) * mm, v(-20.16, 13.77) * mm, v(-18.96, 15) * mm, v(-18.94, 15.03) * mm]});
            skFitSpline(sketch, "E162", {"points": [v(-18.94, 15.03) * mm, v(-18.35, 15.61) * mm, v(-18.35, 16.56) * mm, v(-18.94, 17.15) * mm]});
            skFitSpline(sketch, "E163", {"points": [v(-18.94, 17.15) * mm, v(-19.53, 17.73) * mm, v(-20.47, 17.73) * mm, v(-21.06, 17.15) * mm, v(-21.18, 17.02) * mm, v(-22.83, 15.34) * mm, v(-24.45, 12.26) * mm]});
            skFitSpline(sketch, "E164", {"points": [v(-24.45, 12.26) * mm, v(-25.27, 13.61) * mm, v(-25.72, 14.86) * mm, v(-25.53, 15.8) * mm]});
            skFitSpline(sketch, "E165", {"points": [v(-25.53, 15.8) * mm, v(-25.37, 16.6) * mm, v(-25.9, 17.4) * mm, v(-26.7, 17.56) * mm]});
            skFitSpline(sketch, "E166", {"points": [v(-26.7, 17.56) * mm, v(-27.52, 17.72) * mm, v(-28.3, 17.2) * mm, v(-28.47, 16.38) * mm]});
            skFitSpline(sketch, "E167", {"points": [v(-28.47, 16.38) * mm, v(-28.85, 14.47) * mm, v(-28.04, 12.33) * mm, v(-26.76, 10.29) * mm]});
            skFitSpline(sketch, "E168", {"points": [v(-26.76, 10.29) * mm, v(-28.66, 9.57) * mm, v(-30.33, 8.5) * mm, v(-31.3, 6.88) * mm]});
            skFitSpline(sketch, "E169", {"points": [v(-31.3, 6.88) * mm, v(-31.73, 6.17) * mm, v(-31.5, 5.24) * mm, v(-30.8, 4.82) * mm]});
            skFitSpline(sketch, "E170", {"points": [v(-30.8, 4.82) * mm, v(-30.55, 4.67) * mm, v(-30.28, 4.6) * mm, v(-30.02, 4.6) * mm, v(-29.51, 4.6) * mm, v(-29.01, 4.86) * mm, v(-28.73, 5.33) * mm]});
            skFitSpline(sketch, "E171", {"points": [v(-28.73, 5.33) * mm, v(-28.5, 5.7) * mm, v(-28.2, 6.04) * mm, v(-27.83, 6.34) * mm]});
            skFitSpline(sketch, "E172", {"points": [v(-27.83, 6.34) * mm, v(-27.46, 6.64) * mm, v(-27.02, 6.9) * mm, v(-26.54, 7.13) * mm]});
            skFitSpline(sketch, "E173", {"points": [v(-26.54, 7.13) * mm, v(-26.97, 5.66) * mm, v(-27.31, 4.04) * mm, v(-27.5, 2.27) * mm]});
            skFitSpline(sketch, "E174", {"points": [v(-27.5, 2.27) * mm, v(-27.6, 1.45) * mm, v(-27, 0.7) * mm, v(-26.18, 0.61) * mm]});
            skFitSpline(sketch, "E175", {"points": [v(-26.18, 0.61) * mm, v(-26.13, 0.6) * mm, v(-26.07, 0.6) * mm, v(-26.02, 0.6) * mm, v(-25.26, 0.6) * mm, v(-24.61, 1.17) * mm, v(-24.53, 1.94) * mm]});
            skFitSpline(sketch, "E176", {"points": [v(-24.53, 1.94) * mm, v(-24.35, 3.53) * mm, v(-24.04, 5) * mm, v(-23.65, 6.32) * mm]});
            skFitSpline(sketch, "E177", {"points": [v(-23.65, 6.32) * mm, v(-21.53, 4.03) * mm, v(-19.43, 2.32) * mm, v(-18.96, 1.93) * mm]});
            skFitSpline(sketch, "E178", {"points": [v(-18.96, 1.93) * mm, v(-18.68, 1.71) * mm, v(-18.35, 1.6) * mm, v(-18.02, 1.6) * mm, v(-17.58, 1.6) * mm, v(-17.14, 1.8) * mm, v(-16.85, 2.17) * mm]});
            skFitSpline(sketch, "E179", {"points": [v(-16.85, 2.16) * mm, v(-16.33, 2.8) * mm, v(-16.43, 3.75) * mm, v(-17.08, 4.27) * mm]});
            skFitSpline(sketch, "E180", {"points": [v(-17.06, 4.26) * mm, v(-18.48, 5.4) * mm, v(-20.07, 6.87) * mm, v(-21.5, 8.42) * mm]});
            skFitSpline(sketch, "E181", {"points": [v(-21.5, 8.42) * mm, v(-18.95, 8.73) * mm, v(-16.43, 8.7) * mm, v(-15.12, 8.6) * mm]});
            skFitSpline(sketch, "E182", {"points": [v(-15.12, 8.6) * mm, v(-14.3, 8.53) * mm, v(-13.57, 9.14) * mm, v(-13.5, 9.96) * mm]});
            skFitSpline(sketch, "E183", {"points": [v(-13.5, 9.96) * mm, v(-13.44, 10.79) * mm, v(-14.05, 11.51) * mm, v(-14.88, 11.58) * mm]});
            skLineSegment(sketch, "E184", {"start": v(-68.99, -32.84) * mm, "end": v(-61.18, -32.84) * mm});
            skLineSegment(sketch, "E185", {"start": v(-49.56, 30.71) * mm, "end": v(-41.25, 31.6) * mm});
            skLineSegment(sketch, "E186", {"start": v(-38.05, 33.42) * mm, "end": v(-41.25, 31.6) * mm});
            skLineSegment(sketch, "E187", {"start": v(-19.38, 41.59) * mm, "end": v(-20.25, 44.57) * mm});
            skLineSegment(sketch, "E188", {"start": v(-21.3, 48.93) * mm, "end": v(-20.25, 44.57) * mm});
            skLineSegment(sketch, "E189", {"start": v(22.72, -61.07) * mm, "end": v(25.43, -62.65) * mm});
            skLineSegment(sketch, "E190", {"start": v(25.43, -62.65) * mm, "end": v(26.85, -70.76) * mm});
            skLineSegment(sketch, "E191", {"start": v(56.8, -30.09) * mm, "end": v(56.4, -33.49) * mm});
            skLineSegment(sketch, "E192", {"start": v(56.4, -33.49) * mm, "end": v(60.66, -37.87) * mm});
            skLineSegment(sketch, "E193", {"start": v(84.9, -6.42) * mm, "end": v(87.49, -7.13) * mm});
            skLineSegment(sketch, "E194", {"start": v(87.49, -7.13) * mm, "end": v(92.36, -8.28) * mm});
            skLineSegment(sketch, "E195", {"start": v(66.17, 56.36) * mm, "end": v(61.2, 53.32) * mm});
            skLineSegment(sketch, "E196", {"start": v(61.2, 53.32) * mm, "end": v(58, 52.47) * mm});
            skLineSegment(sketch, "E197", {"start": v(27.98, 41.07) * mm, "end": v(28.65, 32.24) * mm});
            skLineSegment(sketch, "E198", {"start": v(28.65, 32.24) * mm, "end": v(26.04, 30.82) * mm});
            skLineSegment(sketch, "E199", {"start": v(84.57, -16.15) * mm, "end": v(90.97, -13.46) * mm});
            skLineSegment(sketch, "E200", {"start": v(80.58, -22.78) * mm, "end": v(80.89, -29.22) * mm});
            skLineSegment(sketch, "E201", {"start": v(88.6, -21.19) * mm, "end": v(86.59, -23.98) * mm});
            skLineSegment(sketch, "E202", {"start": v(94.6, -20.54) * mm, "end": v(100.05, -19.55) * mm});
            skLineSegment(sketch, "E203", {"start": v(95.37, -22.52) * mm, "end": v(96.43, -27.94) * mm});
            skFitSpline(sketch, "E204", {"points": [v(94.6, -20.54) * mm, v(94.6, -20.54) * mm, v(94.6, -20.54) * mm, v(94.34, -20.43) * mm, v(84.57, -16.14) * mm, v(84.57, -16.14) * mm, v(84.57, -16.14) * mm, v(85.75, -13.56) * mm, v(86.74, -10.62) * mm, v(87.47, -7.23) * mm, v(87.47, -7.2) * mm, v(87.48, -7.16) * mm, v(87.49, -7.13) * mm]});
            skFitSpline(sketch, "E205", {"points": [v(94.6, -20.54) * mm, v(94.6, -20.54) * mm, v(94.6, -20.54) * mm, v(94.34, -20.43) * mm, v(84.57, -16.14) * mm, v(84.57, -16.14) * mm, v(84.57, -16.14) * mm, v(85.75, -13.56) * mm, v(86.74, -10.62) * mm, v(87.47, -7.23) * mm, v(87.47, -7.2) * mm, v(87.48, -7.16) * mm, v(87.49, -7.13) * mm]});
            skLineSegment(sketch, "E206", {"start": v(84.57, -16.14) * mm, "end": v(84.57, -16.15) * mm});
            skSolve(sketch);
        }
        {
            var Q0;
            Q0=qCreatedBy(makeId("Top.planeOp"),FACE);
            var sketch = newSketch(context, id + "F1", { "sketchPlane" : qUnion([Q0])});
            skFitSpline(sketch, "E207", {"points": [v(-49.55, 30.76) * mm, v(-58.43, 46.2) * mm, v(-59.17, 51.62) * mm, v(-59.5, 56.49) * mm, v(-63.27, 63.56) * mm, v(-70.47, 62.83) * mm, v(-72.37, 56.85) * mm, v(-72.34, 52.84) * mm, v(-74.6, 45.55) * mm, v(-81.8, 40.59) * mm, v(-93.96, 43) * mm, v(-100.24, 59.82) * mm], "startDerivative": vector(-122.72, 107.54) * mm, "endDerivative": vector(-0.7, 133) * mm});
            skFitSpline(sketch, "E208", {"points": [v(-100.24, 59.82) * mm, v(-99.25, 71.44) * mm, v(-93.42, 82.73) * mm, v(-83.15, 90.09) * mm, v(-69.24, 93.22) * mm, v(-53.94, 91.83) * mm, v(-43.4, 86.28) * mm, v(-35.95, 76.83) * mm, v(-32.19, 63.95) * mm, v(-30.56, 54.25) * mm, v(-26.86, 49.4) * mm, v(-19.81, 49.16) * mm, v(-9.25, 50.01) * mm, v(1.57, 49.88) * mm, v(14.24, 47.33) * mm, v(28, 41.02) * mm], "startDerivative": vector(0.56, 172.82) * mm, "endDerivative": vector(193.98, -117.47) * mm});
            skFitSpline(sketch, "E209", {"points": [v(28, 41.02) * mm, v(36.54, 50.06) * mm, v(44.19, 56) * mm, v(51.67, 59.5) * mm, v(58.48, 60.27) * mm, v(63.86, 58.9) * mm, v(66.43, 55.4) * mm, v(66.53, 50.64) * mm, v(66.24, 45.61) * mm], "startDerivative": vector(47.82, 56.6) * mm, "endDerivative": vector(-3.58, -61.82) * mm});
            skFitSpline(sketch, "E210", {"points": [v(66.24, 45.61) * mm, v(74.07, 49.41) * mm, v(80.44, 50.76) * mm, v(85.59, 48.28) * mm, v(88.1, 43.44) * mm, v(88.5, 37.77) * mm, v(87.49, 30.97) * mm, v(86.87, 25.86) * mm, v(86.41, 18.5) * mm], "startDerivative": vector(54.4, 28.33) * mm, "endDerivative": vector(-3.16, -57.98) * mm});
            skFitSpline(sketch, "E211", {"points": [v(86.41, 18.5) * mm, v(88.9, 13.82) * mm, v(91.16, 7.88) * mm, v(92.6, 0.96) * mm, v(92.75, -4.07) * mm, v(92.23, -8.94) * mm, v(90.98, -13.47) * mm], "startDerivative": vector(15.62, -27.88) * mm, "endDerivative": vector(-9.24, -29.02) * mm});
            skFitSpline(sketch, "E212", {"points": [v(90.98, -13.47) * mm, v(96.39, -15.85) * mm, v(98.98, -17.66) * mm, v(100.4, -20.6) * mm, v(100.03, -24.4) * mm, v(98.51, -26.63) * mm, v(96.45, -27.96) * mm], "startDerivative": vector(27.06, -11.29) * mm, "endDerivative": vector(-15.48, -8.44) * mm});
            skFitSpline(sketch, "E213", {"points": [v(96.45, -27.96) * mm, v(96.12, -30.56) * mm, v(94.38, -33.2) * mm, v(91.08, -34.83) * mm, v(86.82, -34.14) * mm, v(84.86, -32.63) * mm, v(80.9, -29.2) * mm], "startDerivative": vector(-0.54, -18.16) * mm, "endDerivative": vector(-21.9, 18.45) * mm});
            skFitSpline(sketch, "E214", {"points": [v(80.9, -29.2) * mm, v(78.11, -31.46) * mm, v(73.57, -34.24) * mm, v(67.43, -36.62) * mm, v(63.63, -37.49) * mm, v(60.64, -37.86) * mm], "startDerivative": vector(-14.5, -12.35) * mm, "endDerivative": vector(-17.85, -1.93) * mm});
            skFitSpline(sketch, "E215", {"points": [v(60.64, -37.86) * mm, v(59.83, -42.56) * mm, v(59.02, -45.9) * mm, v(57.84, -49.18) * mm, v(56.84, -51.97) * mm, v(56.02, -54.85) * mm, v(55.13, -58.32) * mm, v(54.14, -63.11) * mm], "startDerivative": vector(-4.87, -30.39) * mm, "endDerivative": vector(-6.83, -33.35) * mm});
            skFitSpline(sketch, "E216", {"points": [v(54.14, -63.11) * mm, v(56.94, -66.55) * mm, v(58.48, -72.73) * mm, v(57.09, -77.57) * mm, v(53.21, -81.74) * mm, v(47.41, -84.42) * mm, v(38.94, -84.63) * mm, v(32.46, -81.23) * mm, v(29.14, -76.71) * mm, v(27.58, -73.1) * mm, v(26.81, -70.76) * mm], "startDerivative": vector(33.46, -32.98) * mm, "endDerivative": vector(-10.07, 33.17) * mm});
            skFitSpline(sketch, "E217", {"points": [v(26.81, -70.76) * mm, v(24.1, -75.8) * mm, v(20.64, -80.96) * mm, v(16.65, -85.62) * mm, v(10.9, -90.18) * mm, v(4.44, -92.68) * mm, v(-2.97, -92.86) * mm, v(-8.2, -90.28) * mm, v(-12.25, -84.38) * mm, v(-13.02, -77.56) * mm, v(-11.65, -71.22) * mm, v(-9.23, -64.27) * mm, v(-8.02, -61.05) * mm], "startDerivative": vector(-32.58, -63.74) * mm, "endDerivative": vector(17.75, 46.77) * mm});
            skFitSpline(sketch, "E218", {"points": [v(-8.02, -61.05) * mm, v(-14.25, -61.21) * mm, v(-19.74, -61.05) * mm, v(-25, -60.54) * mm, v(-27.81, -60.03) * mm], "startDerivative": vector(-22.47, -0.8) * mm, "endDerivative": vector(-13.46, 2.73) * mm});
            skFitSpline(sketch, "E219", {"points": [v(-27.81, -60.03) * mm, v(-25.5, -66.94) * mm, v(-24.12, -71.09) * mm, v(-23.46, -75.64) * mm, v(-23.9, -81.07) * mm, v(-25.44, -84.82) * mm, v(-28.53, -88.29) * mm, v(-32.56, -90.23) * mm, v(-37.03, -90.43) * mm, v(-41.57, -89.37) * mm, v(-46.56, -86.54) * mm, v(-52.88, -80.55) * mm, v(-56.53, -75.51) * mm, v(-62.42, -63.89) * mm, v(-67.9, -42.2) * mm, v(-69.25, -21.33) * mm, v(-66.13, 0) * mm, v(-60.45, 14.53) * mm, v(-55.13, 23.72) * mm, v(-49.55, 30.76) * mm], "startDerivative": vector(49.65, -151.6) * mm, "endDerivative": vector(106.1, 125.73) * mm});
            skSolve(sketch);
        }
        {
            var Q0;
            Q0=makeQuery(id+"F1.imprint","IMPRINT",FACE,{"disambiguationData":[TD([[makeQuery(id+"F1.imprint","IMPRINT",EDGE,{"derivedFrom":sQuery(id+"F1.wireOp",EDGE,"E207")}),-1.0]])]});
            extrude(context, id + "F2", {"entities" : qUnion([Q0]), "depth" : 4 * mm, "offsetDistance" : 25 * mm});
        }
        {
            var Q0;
            {var subQ5=sQuery(id+"F0.wireOp",EDGE,"E107");Q0=makeQuery(id+"F0.imprint","IMPRINT",FACE,{"disambiguationData":[TD([[makeQuery(id+"F0.imprint","IMPRINT",EDGE,{"derivedFrom":subQ5}),-1.0]])]});}
            extrude(context, id + "F3", {"entities" : qUnion([Q0]), "operationType" : NewBodyOperationType.REMOVE, "depth" : 4 * mm, "offsetDistance" : 25 * mm});
        }
        {
            var Q0;
            {var subQ5=sQuery(id+"F0.wireOp",EDGE,"E107");Q0=makeQuery(id+"F0.imprint","IMPRINT",FACE,{"disambiguationData":[TD([[makeQuery(id+"F0.imprint","IMPRINT",EDGE,{"derivedFrom":subQ5}),-1.0]])]});}
            extrude(context, id + "F4", {"entities" : qUnion([Q0]), "operationType" : NewBodyOperationType.ADD, "depth" : 3 * mm, "offsetDistance" : 25 * mm});
        }
        {
            var Q0;
            Q0=makeQuery(id+"F0.imprint","IMPRINT",FACE,{"disambiguationData":[TD([[makeQuery(id+"F0.imprint","IMPRINT",EDGE,{"derivedFrom":sQuery(id+"F0.wireOp",EDGE,"E144")}),1.0]])]});
            var Q1;
            Q1=makeQuery(id+"F0.imprint","IMPRINT",FACE,{"disambiguationData":[TD([[makeQuery(id+"F0.imprint","IMPRINT",EDGE,{"derivedFrom":sQuery(id+"F0.wireOp",EDGE,"E143")}),1.0]])]});
            var Q2;
            Q2=makeQuery(id+"F0.imprint","IMPRINT",FACE,{"disambiguationData":[TD([[makeQuery(id+"F0.imprint","IMPRINT",EDGE,{"derivedFrom":sQuery(id+"F0.wireOp",EDGE,"E145")}),1.0]])]});
            var Q3;
            Q3=makeQuery(id+"F0.imprint","IMPRINT",FACE,{"disambiguationData":[TD([[makeQuery(id+"F0.imprint","IMPRINT",EDGE,{"derivedFrom":sQuery(id+"F0.wireOp",EDGE,"E160")}),1.0]])]});
            extrude(context, id + "F5", {"entities" : qUnion([Q0, Q1, Q2, Q3]), "operationType" : NewBodyOperationType.ADD, "depth" : 8 * mm, "offsetDistance" : 25 * mm});
        }
        {
            var Q0;
            Q0=makeQuery(id+"F0.imprint","IMPRINT",FACE,{"disambiguationData":[TD([[makeQuery(id+"F0.imprint","IMPRINT",EDGE,{"derivedFrom":sQuery(id+"F0.wireOp",EDGE,"E50")}),1.0]])]});
            var Q1;
            {var subQ4=sQuery(id+"F0.wireOp",EDGE,"E117");Q1=makeQuery(id+"F0.imprint","IMPRINT",FACE,{"disambiguationData":[TD([[makeQuery(id+"F0.imprint","IMPRINT",EDGE,{"derivedFrom":subQ4}),1.0]])]});}
            var Q2;
            Q2=makeQuery(id+"F0.imprint","IMPRINT",FACE,{"disambiguationData":[TD([[makeQuery(id+"F0.imprint","IMPRINT",EDGE,{"derivedFrom":sQuery(id+"F0.wireOp",EDGE,"E49")}),1.0]])]});
            var Q3;
            {var subQ1=sQuery(id+"F0.wireOp",EDGE,"E48");Q3=makeQuery(id+"F0.imprint","IMPRINT",FACE,{"disambiguationData":[TD([[makeQuery(id+"F0.imprint","IMPRINT",EDGE,{"derivedFrom":subQ1}),1.0]])]});}
            var Q4;
            Q4=makeQuery(id+"F0.imprint","IMPRINT",FACE,{"disambiguationData":[TD([[makeQuery(id+"F0.imprint","IMPRINT",EDGE,{"derivedFrom":sQuery(id+"F0.wireOp",EDGE,"E44")}),1.0]])]});
            var Q5;
            Q5=makeQuery(id+"F0.imprint","IMPRINT",FACE,{"disambiguationData":[TD([[makeQuery(id+"F0.imprint","IMPRINT",EDGE,{"derivedFrom":sQuery(id+"F0.wireOp",EDGE,"E71")}),1.0]])]});
            var Q6;
            {var subQ9=sQuery(id+"F0.wireOp",EDGE,"E41");Q6=makeQuery(id+"F0.imprint","IMPRINT",FACE,{"disambiguationData":[TD([[makeQuery(id+"F0.imprint","IMPRINT",EDGE,{"derivedFrom":subQ9}),-1.0]])]});}
            var Q7;
            {var subQ4=sQuery(id+"F0.wireOp",EDGE,"E41");Q7=makeQuery(id+"F0.imprint","IMPRINT",FACE,{"disambiguationData":[TD([[makeQuery(id+"F0.imprint","IMPRINT",EDGE,{"derivedFrom":subQ4}),1.0]])]});}
            extrude(context, id + "F6", {"entities" : qUnion([Q0, Q1, Q2, Q3, Q4, Q5, Q6, Q7]), "operationType" : NewBodyOperationType.ADD, "depth" : 8 * mm, "offsetDistance" : 25 * mm});
        }
        {
            var Q0;
            Q0=qCreatedBy(makeId("Top.planeOp"),FACE);
            var sketch = newSketch(context, id + "F7", { "sketchPlane" : qUnion([Q0])});
            skFitSpline(sketch, "E220", {"points": [v(56.77, -30.05) * mm, v(65.25, -29.29) * mm, v(74.08, -25.13) * mm, v(81.4, -16.3) * mm, v(84, -9.88) * mm, v(84.9, -6.42) * mm], "startDerivative": vector(40.81, -3.88) * mm, "endDerivative": vector(6.2, 29.7) * mm});
            skFitSpline(sketch, "E221", {"points": [v(87.49, -7.13) * mm, v(86.67, -10.53) * mm, v(85.56, -13.7) * mm, v(84.64, -16.14) * mm, v(82.87, -19.37) * mm, v(80.5, -22.9) * mm, v(75.32, -27.93) * mm, v(68.72, -31.5) * mm, v(60.9, -33.37) * mm, v(56.14, -33.46) * mm], "startDerivative": vector(-8.63, -39.7) * mm, "endDerivative": vector(-40.2, 1.48) * mm});
            skLineSegment(sketch, "E222", {"start": v(56.77, -30.05) * mm, "end": v(56.14, -33.46) * mm});
            skLineSegment(sketch, "E223", {"start": v(84.9, -6.42) * mm, "end": v(87.49, -7.13) * mm});
            skFitSpline(sketch, "E224", {"points": [v(84.64, -16.14) * mm, v(94.58, -20.56) * mm, v(95.41, -21.25) * mm, v(95.46, -22.36) * mm, v(94.84, -23.16) * mm, v(93.81, -23.42) * mm, v(93.14, -23.16) * mm, v(83.2, -18.82) * mm], "startDerivative": vector(44.26, -19.12) * mm, "endDerivative": vector(-45.74, 19.5) * mm});
            skFitSpline(sketch, "E225", {"points": [v(82.3, -20.3) * mm, v(90.99, -27.77) * mm, v(91.1, -27.88) * mm, v(91.43, -28.47) * mm, v(91.41, -29.49) * mm, v(90.95, -30.06) * mm, v(90.37, -30.38) * mm, v(89.6, -30.36) * mm, v(88.94, -30) * mm, v(88.55, -29.67) * mm, v(80.59, -22.78) * mm], "startDerivative": vector(46.92, -40.32) * mm, "endDerivative": vector(-42.57, 36.56) * mm});
            skSolve(sketch);
        }
        {
            var Q0;
            {var subQ0=sQuery(id+"F7.wireOp",EDGE,"E225");Q0=makeQuery(id+"F7.imprint","IMPRINT",FACE,{"disambiguationData":[TD([[makeQuery(id+"F7.imprint","IMPRINT",EDGE,{"derivedFrom":subQ0}),-1.0]])]});}
            var Q1;
            {var subQ0=sQuery(id+"F7.wireOp",EDGE,"E224");Q1=makeQuery(id+"F7.imprint","IMPRINT",FACE,{"disambiguationData":[TD([[makeQuery(id+"F7.imprint","IMPRINT",EDGE,{"derivedFrom":subQ0}),-1.0]])]});}
            var Q2;
            Q2=makeQuery(id+"F7.imprint","IMPRINT",FACE,{"disambiguationData":[TD([[makeQuery(id+"F7.imprint","IMPRINT",EDGE,{"derivedFrom":sQuery(id+"F7.wireOp",EDGE,"E220")}),-1.0]])]});
            extrude(context, id + "F8", {"entities" : qUnion([Q0, Q1, Q2]), "operationType" : NewBodyOperationType.ADD, "depth" : 8 * mm, "offsetDistance" : 25 * mm});
        }
    });
